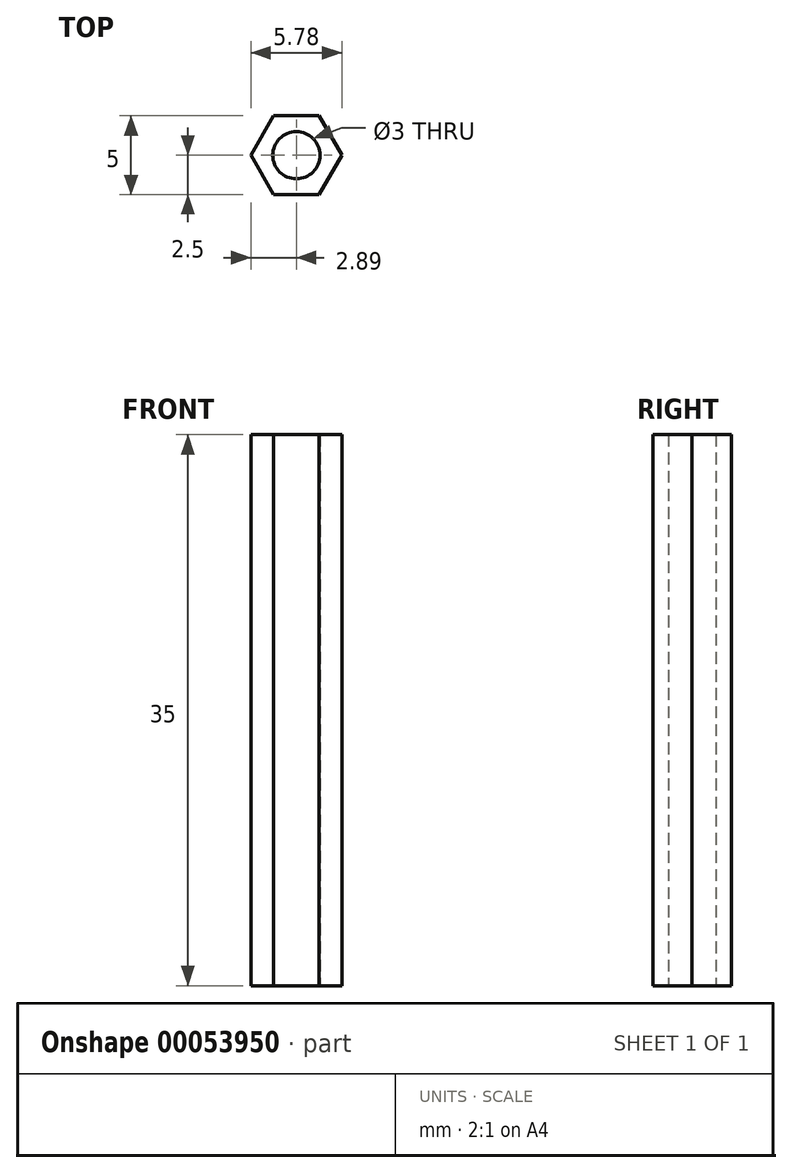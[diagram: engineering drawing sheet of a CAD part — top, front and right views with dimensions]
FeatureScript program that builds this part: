
annotation { "Feature Type Name" : "Feature", "Feature Type Description" : "" }
export const myFeature = defineFeature(function(context is Context, id is Id, definition is map)
    precondition{}
    {
        {
            var Q0;
            Q0=qCreatedBy(makeId("Top.planeOp"),FACE);
            var sketch = newSketch(context, id + "F0", { "sketchPlane" : qUnion([Q0])});
            skCircle(sketch, "E0.cCircle", {"center": v(0, 0) * mm, "radius": 2.5 * mm, "construction": true});
            skLineSegment(sketch, "E0.0", {"start": v(1.44, -2.5) * mm, "end": v(-1.44, -2.5) * mm});
            skLineSegment(sketch, "E0.1", {"start": v(-1.44, -2.5) * mm, "end": v(-2.89, 0) * mm});
            skLineSegment(sketch, "E0.2", {"start": v(-2.89, 0) * mm, "end": v(-1.44, 2.5) * mm});
            skLineSegment(sketch, "E0.3", {"start": v(-1.44, 2.5) * mm, "end": v(1.44, 2.5) * mm});
            skLineSegment(sketch, "E0.4", {"start": v(1.44, 2.5) * mm, "end": v(2.89, 0) * mm});
            skLineSegment(sketch, "E0.5", {"start": v(2.89, 0) * mm, "end": v(1.44, -2.5) * mm});
            skPoint(sketch, "E0.0.midPoint", {"position": v(0, -2.5) * mm});
            skCircle(sketch, "E1", {"center": v(0, 0) * mm, "radius": 1.5 * mm});
            skSolve(sketch);
        }
        {
            var Q0;
            Q0 = qSketchRegion(id + "F0", true);
            extrude(context, id + "F1", {"entities" : qUnion([Q0]), "depth" : 35 * mm});
        }
    });
